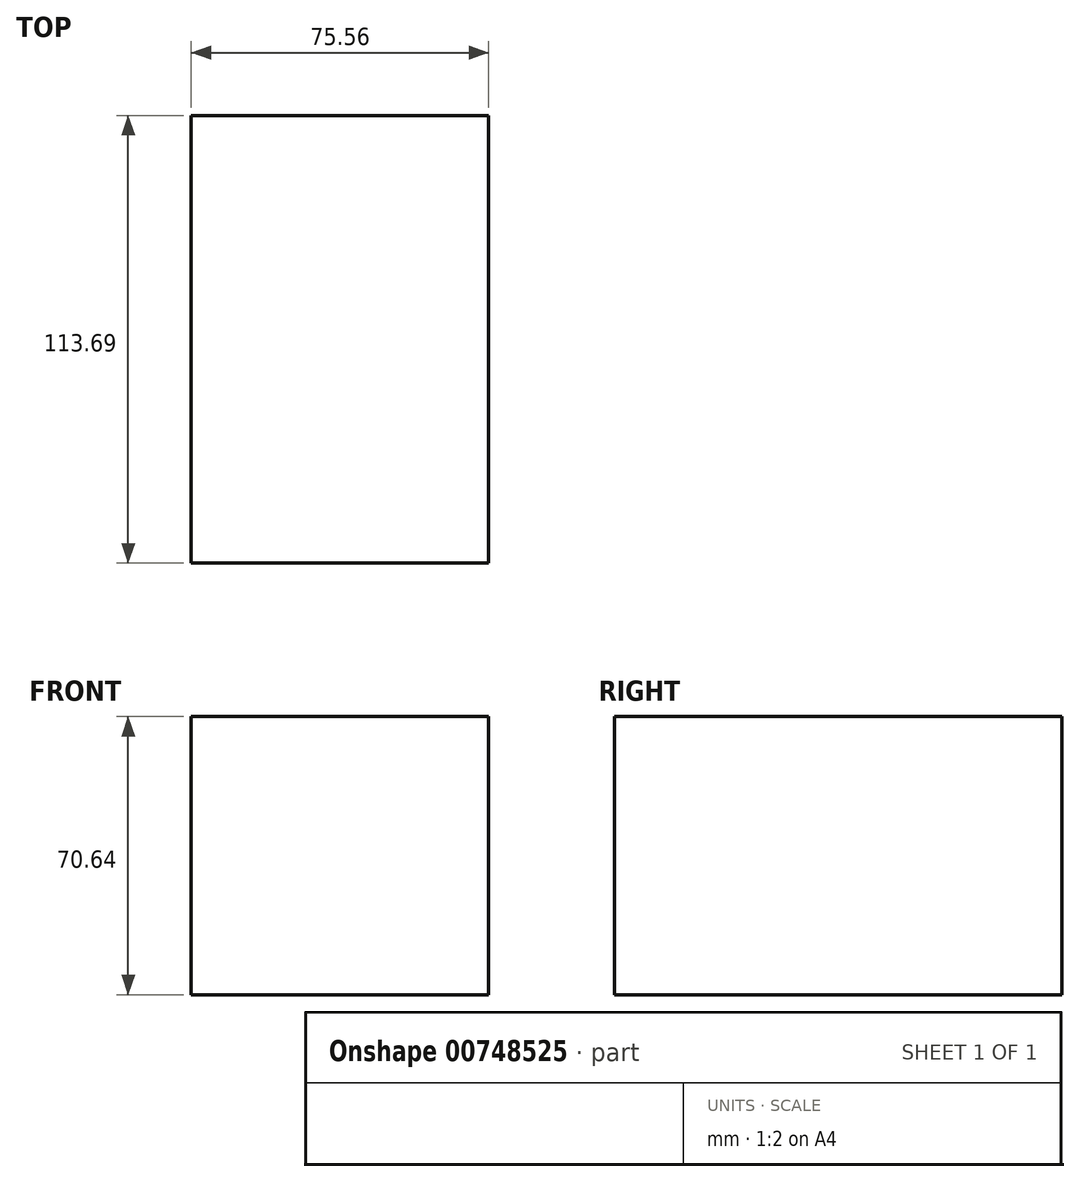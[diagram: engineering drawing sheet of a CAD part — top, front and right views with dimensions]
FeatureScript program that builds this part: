
annotation { "Feature Type Name" : "Feature", "Feature Type Description" : "" }
export const myFeature = defineFeature(function(context is Context, id is Id, definition is map)
    precondition{}
    {
        {
            var Q0;
            Q0=qCreatedBy(makeId("Front.planeOp"),FACE);
            var sketch = newSketch(context, id + "F0", { "sketchPlane" : qUnion([Q0])});
            skLineSegment(sketch, "E0.bottom", {"start": v(37.78, 35.32) * mm, "end": v(-37.78, 35.32) * mm});
            skLineSegment(sketch, "E0.top", {"start": v(37.78, -35.32) * mm, "end": v(-37.78, -35.32) * mm});
            skLineSegment(sketch, "E0.left", {"start": v(37.78, 35.32) * mm, "end": v(37.78, -35.32) * mm});
            skLineSegment(sketch, "E0.right", {"start": v(-37.78, 35.32) * mm, "end": v(-37.78, -35.32) * mm});
            skPoint(sketch, "E0.middle", {"position": v(0, 0) * mm});
            skSolve(sketch);
        }
        {
            var Q0;
            Q0=makeQuery(id+"F0.imprint","IMPRINT",FACE,{"disambiguationData":[TD([[makeQuery(id+"F0.imprint","IMPRINT",EDGE,{"derivedFrom":sQuery(id+"F0.wireOp",EDGE,"E0.bottom")}),1.0]])]});
            extrude(context, id + "F1", {"entities" : qUnion([Q0]), "depth" : 113.7 * mm, "offsetDistance" : 25 * mm});
        }
    });
